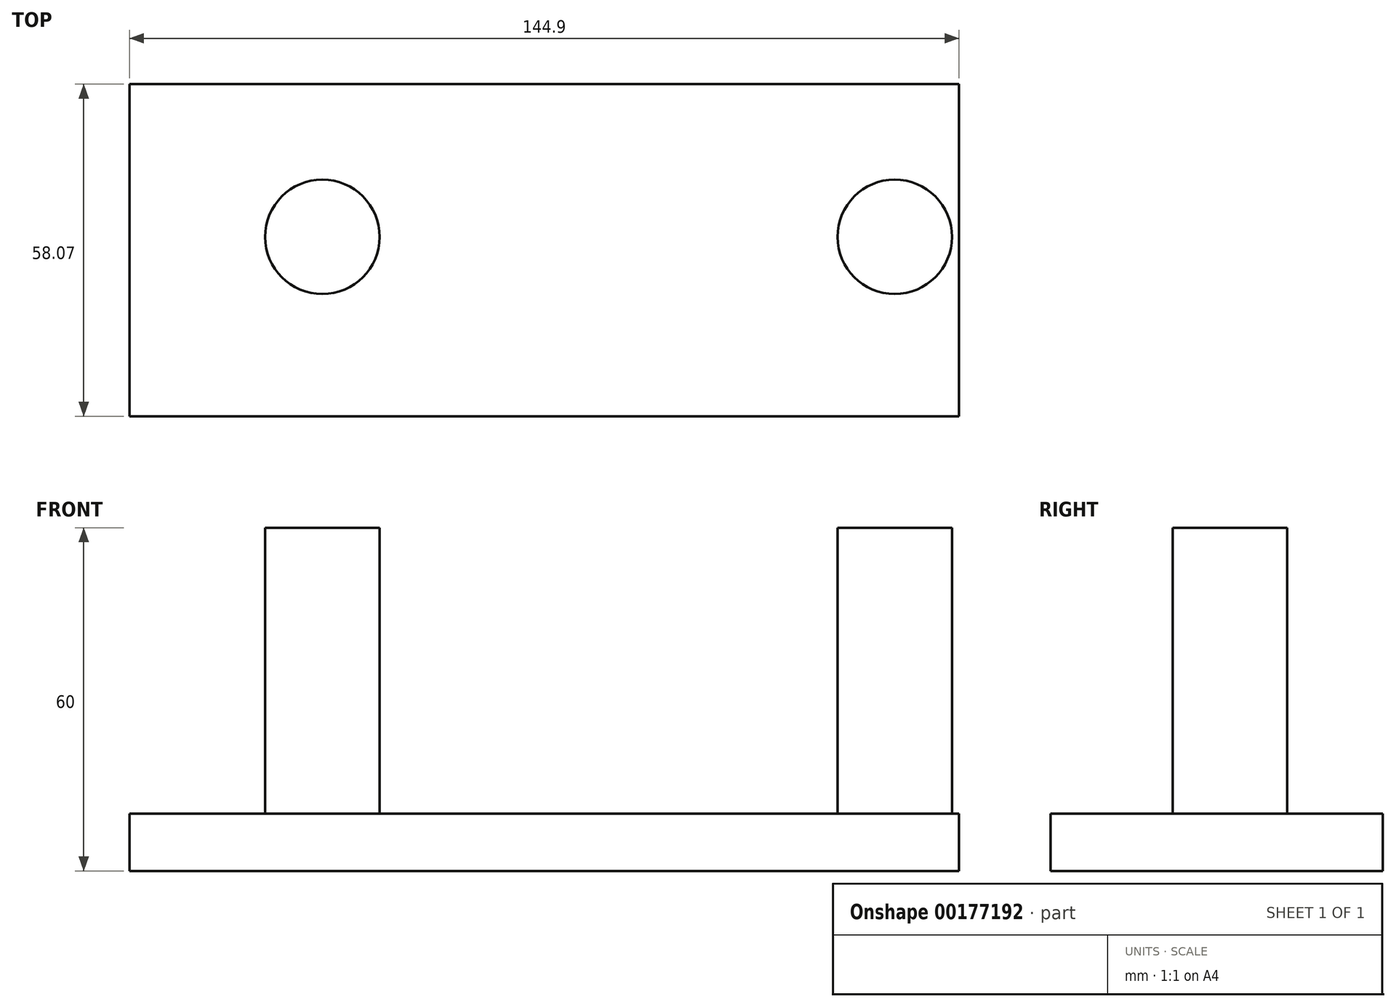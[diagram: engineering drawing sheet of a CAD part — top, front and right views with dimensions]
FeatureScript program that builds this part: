
annotation { "Feature Type Name" : "Feature", "Feature Type Description" : "" }
export const myFeature = defineFeature(function(context is Context, id is Id, definition is map)
    precondition{}
    {
        {
            var Q0;
            Q0=qCreatedBy(makeId("Top.planeOp"),FACE);
            var sketch = newSketch(context, id + "F0", { "sketchPlane" : qUnion([Q0])});
            skLineSegment(sketch, "E0.bottom", {"start": v(-73.68, 26.7) * mm, "end": v(71.22, 26.7) * mm});
            skLineSegment(sketch, "E0.top", {"start": v(-73.68, -31.36) * mm, "end": v(71.22, -31.36) * mm});
            skLineSegment(sketch, "E0.left", {"start": v(-73.68, 26.7) * mm, "end": v(-73.68, -31.36) * mm});
            skLineSegment(sketch, "E0.right", {"start": v(71.22, 26.7) * mm, "end": v(71.22, -31.36) * mm});
            skSolve(sketch);
        }
        {
            var Q0;
            Q0 = qSketchRegion(id + "F0", true);
            extrude(context, id + "F1", {"entities" : qUnion([Q0]), "depth" : 10 * mm});
        }
        {
            var Q0;
            Q0=makeQuery(id+"F1.opExtrude","CAP_FACE",FACE,{"disambiguationData":[OSD([sQuery(id+"F0.wireOp",EDGE,"E0.bottom"),sQuery(id+"F0.wireOp",EDGE,"E0.top"),sQuery(id+"F0.wireOp",EDGE,"E0.left"),sQuery(id+"F0.wireOp",EDGE,"E0.right")])],"isStart":false});
            var sketch = newSketch(context, id + "F2", { "sketchPlane" : qUnion([Q0])});
            skCircle(sketch, "E1", {"center": v(-40, 0) * mm, "radius": 10 * mm});
            skCircle(sketch, "E2", {"center": v(60, 0) * mm, "radius": 10 * mm});
            skSolve(sketch);
        }
        {
            var Q0;
            Q0 = qSketchRegion(id + "F2", true);
            extrude(context, id + "F3", {"entities" : qUnion([Q0]), "operationType" : NewBodyOperationType.ADD, "depth" : 50 * mm});
        }
    });
